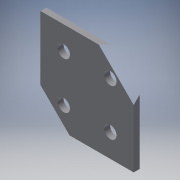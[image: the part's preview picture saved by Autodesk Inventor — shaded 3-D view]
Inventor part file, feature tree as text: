
AUTODESK INVENTOR PART (.ipt)
format: ipt  version: 2016 (Build 200138000, 138)  size: 107,008 bytes
history: native  units: in
note: dims shown in document units (in); Inventor stores cm internally (conversion verified against a paired STEP export)
features: extrude x1, sketch x1
ambient origin geometry x8: Origin, YZ Plane, XZ Plane, XY Plane, X Axis, Y Axis, Z Axis, Center Point
bodies: Body1 (feature_tree)
feature tree (2):
  extrude  "Extrusion2"  Depth=0.125in
  sketch  "Sketch1"  dims[d0=2.0in d1=1.0in d2=3.0in d3=2.0in d4=0.2656in d5=1.5in d6=0.5in d7=1.5in d9=0.5in d10=0.5in d14=0.5in d15=0.5in d16=0.125in d17=0.0in d18=0.5in]
